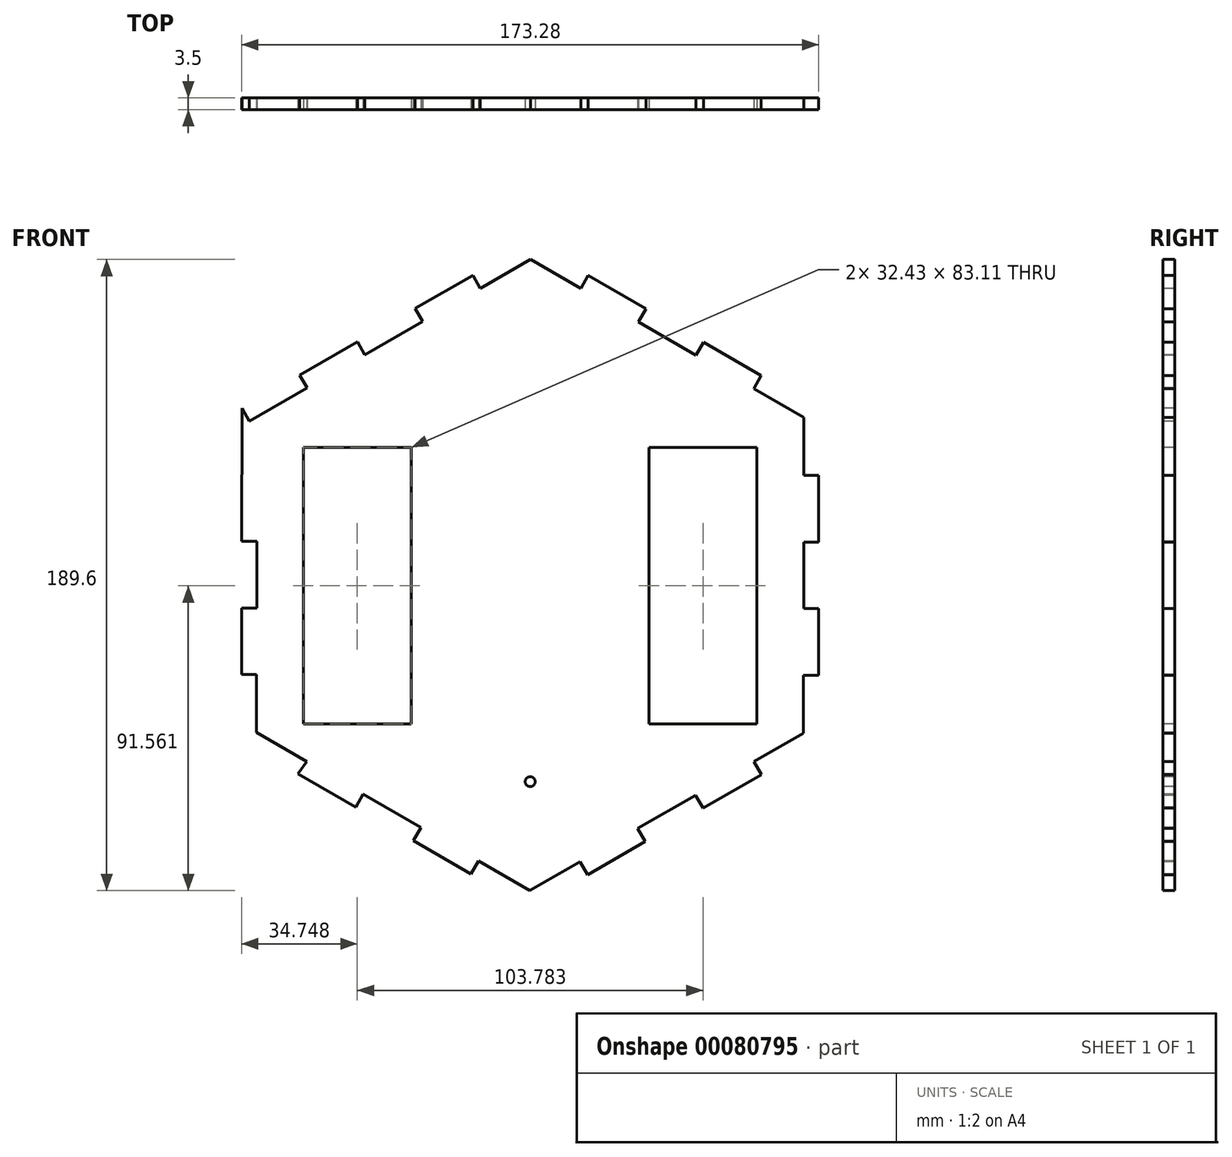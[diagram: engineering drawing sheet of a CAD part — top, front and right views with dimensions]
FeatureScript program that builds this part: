
annotation { "Feature Type Name" : "Feature", "Feature Type Description" : "" }
export const myFeature = defineFeature(function(context is Context, id is Id, definition is map)
    precondition{}
    {
        {
            var Q0;
            Q0=qCreatedBy(makeId("Front.planeOp"),FACE);
            var sketch = newSketch(context, id + "F0", { "sketchPlane" : qUnion([Q0])});
            skCircle(sketch, "E0.cCircle", {"center": v(0, 0) * mm, "radius": 86.6 * mm, "construction": true});
            skLineSegment(sketch, "E0.0", {"start": v(-86.54, 50.12) * mm, "end": v(0.13, 100) * mm});
            skLineSegment(sketch, "E0.1", {"start": v(0.13, 100) * mm, "end": v(86.67, 49.88) * mm});
            skLineSegment(sketch, "E0.2", {"start": v(86.67, 49.88) * mm, "end": v(86.54, -50.12) * mm});
            skLineSegment(sketch, "E0.3", {"start": v(86.54, -50.12) * mm, "end": v(-0.13, -100) * mm});
            skLineSegment(sketch, "E0.4", {"start": v(-0.13, -100) * mm, "end": v(-86.67, -49.88) * mm});
            skLineSegment(sketch, "E0.5", {"start": v(-86.67, -49.88) * mm, "end": v(-86.54, 50.12) * mm});
            skPoint(sketch, "E0.0.midPoint", {"position": v(-43.2, 75.06) * mm});
            skSolve(sketch);
        }
        {
            var Q0;
            Q0=makeQuery(id+"F0.imprint","IMPRINT",FACE,{"disambiguationData":[TD([[makeQuery(id+"F0.imprint","IMPRINT",EDGE,{"derivedFrom":sQuery(id+"F0.wireOp",EDGE,"E0.0")}),-1.0]])]});
            extrude(context, id + "F1", {"entities" : qUnion([Q0]), "depth" : 3.5 * mm});
        }
        {
            var Q0;
            Q0=makeQuery(id+"F1.opExtrude","CAP_FACE",FACE,{"disambiguationData":[OSD([sQuery(id+"F0.wireOp",EDGE,"E0.0"),sQuery(id+"F0.wireOp",EDGE,"E0.1"),sQuery(id+"F0.wireOp",EDGE,"E0.2"),sQuery(id+"F0.wireOp",EDGE,"E0.3"),sQuery(id+"F0.wireOp",EDGE,"E0.4"),sQuery(id+"F0.wireOp",EDGE,"E0.5")])],"isStart":false});
            var sketch = newSketch(context, id + "F2", { "sketchPlane" : qUnion([Q0])});
            skLineSegment(sketch, "E1", {"start": v(-86.54, 50.12) * mm, "end": v(-84.3, 46.22) * mm});
            skLineSegment(sketch, "E2", {"start": v(-84.3, 46.22) * mm, "end": v(-66.96, 56.2) * mm});
            skLineSegment(sketch, "E3", {"start": v(-66.96, 56.2) * mm, "end": v(-69.2, 60.1) * mm});
            skLineSegment(sketch, "E4", {"start": v(-69.2, 60.1) * mm, "end": v(-51.87, 70.07) * mm});
            skLineSegment(sketch, "E5", {"start": v(-51.87, 70.07) * mm, "end": v(-49.62, 66.17) * mm});
            skLineSegment(sketch, "E6", {"start": v(-49.62, 66.17) * mm, "end": v(-32.29, 76.15) * mm});
            skLineSegment(sketch, "E7", {"start": v(-32.29, 76.15) * mm, "end": v(-34.53, 80.05) * mm});
            skLineSegment(sketch, "E8", {"start": v(-34.53, 80.05) * mm, "end": v(-17.2, 90.02) * mm});
            skLineSegment(sketch, "E9", {"start": v(-17.2, 90.02) * mm, "end": v(-17.2, 90.02) * mm});
            skLineSegment(sketch, "E10", {"start": v(-17.2, 90.02) * mm, "end": v(0.13, 100) * mm});
            skLineSegment(sketch, "E11", {"start": v(0.13, 100) * mm, "end": v(2.38, 96.1) * mm});
            skLineSegment(sketch, "E12", {"start": v(-17.2, 90.02) * mm, "end": v(-14.95, 86.12) * mm});
            skLineSegment(sketch, "E13", {"start": v(-14.95, 86.12) * mm, "end": v(2.38, 96.1) * mm});
            skLineSegment(sketch, "E14", {"start": v(-86.67, -49.88) * mm, "end": v(-82.14, -49.89) * mm});
            skLineSegment(sketch, "E15", {"start": v(-82.14, -49.89) * mm, "end": v(-82.14, -29.89) * mm});
            skLineSegment(sketch, "E16", {"start": v(-82.14, -29.89) * mm, "end": v(-86.64, -29.88) * mm});
            skLineSegment(sketch, "E17", {"start": v(-86.64, -29.88) * mm, "end": v(-86.62, -9.88) * mm});
            skLineSegment(sketch, "E18", {"start": v(-86.6, 0) * mm, "end": v(-86.58, 20) * mm});
            skLineSegment(sketch, "E19", {"start": v(-81.27, 30.12) * mm, "end": v(-86.56, 30.12) * mm});
            skLineSegment(sketch, "E20", {"start": v(-86.67, -49.88) * mm, "end": v(-86.67, -49.88) * mm});
            skLineSegment(sketch, "E21", {"start": v(-86.56, 30.12) * mm, "end": v(-86.54, 50.12) * mm});
            skLineSegment(sketch, "E22", {"start": v(-86.62, -9.88) * mm, "end": v(-82.12, -9.89) * mm});
            skLineSegment(sketch, "E23", {"start": v(-82.12, -9.89) * mm, "end": v(-82.12, 10.11) * mm});
            skLineSegment(sketch, "E24", {"start": v(-82.12, 10.11) * mm, "end": v(-86.59, 10.12) * mm});
            skLineSegment(sketch, "E25", {"start": v(-86.59, 10.12) * mm, "end": v(-86.56, 30.12) * mm});
            skLineSegment(sketch, "E26", {"start": v(-86.56, 30.12) * mm, "end": v(-82.06, 30.11) * mm});
            skLineSegment(sketch, "E27", {"start": v(-82.06, 30.11) * mm, "end": v(-82.06, 50.11) * mm});
            skLineSegment(sketch, "E28", {"start": v(-82.06, 50.11) * mm, "end": v(-86.54, 50.11) * mm});
            skLineSegment(sketch, "E29", {"start": v(-86.54, 50.11) * mm, "end": v(-86.54, 50.12) * mm});
            skLineSegment(sketch, "E30", {"start": v(86.54, -50.12) * mm, "end": v(82.06, -50.11) * mm});
            skLineSegment(sketch, "E31", {"start": v(82.06, -50.11) * mm, "end": v(82.06, -30.11) * mm});
            skLineSegment(sketch, "E32", {"start": v(82.06, -30.11) * mm, "end": v(86.56, -30.11) * mm});
            skLineSegment(sketch, "E33", {"start": v(86.56, -30.11) * mm, "end": v(86.59, -10.11) * mm});
            skLineSegment(sketch, "E34", {"start": v(86.59, -10.11) * mm, "end": v(82.09, -10.1) * mm});
            skLineSegment(sketch, "E35", {"start": v(82.09, -10.1) * mm, "end": v(82.09, 9.9) * mm});
            skLineSegment(sketch, "E36", {"start": v(82.09, 9.9) * mm, "end": v(86.62, 9.89) * mm});
            skLineSegment(sketch, "E37", {"start": v(86.62, 9.89) * mm, "end": v(86.64, 29.89) * mm});
            skLineSegment(sketch, "E38", {"start": v(86.64, 29.89) * mm, "end": v(82.14, 29.9) * mm});
            skLineSegment(sketch, "E39", {"start": v(82.14, 29.9) * mm, "end": v(82.14, 49.9) * mm});
            skLineSegment(sketch, "E40", {"start": v(82.14, 49.9) * mm, "end": v(86.67, 49.89) * mm});
            skLineSegment(sketch, "E41", {"start": v(86.67, 49.88) * mm, "end": v(86.67, 49.89) * mm});
            skLineSegment(sketch, "E42", {"start": v(86.54, -50.12) * mm, "end": v(86.54, -50.12) * mm});
            skLineSegment(sketch, "E43", {"start": v(43.43, 74.93) * mm, "end": v(0.13, 100) * mm});
            skLineSegment(sketch, "E44", {"start": v(86.67, 49.89) * mm, "end": v(84.41, 46) * mm});
            skLineSegment(sketch, "E45", {"start": v(84.41, 46) * mm, "end": v(67.1, 56.01) * mm});
            skLineSegment(sketch, "E46", {"start": v(67.1, 56.01) * mm, "end": v(69.36, 59.9) * mm});
            skLineSegment(sketch, "E47", {"start": v(69.36, 59.9) * mm, "end": v(52.05, 69.93) * mm});
            skLineSegment(sketch, "E48", {"start": v(52.05, 69.93) * mm, "end": v(49.8, 66.04) * mm});
            skLineSegment(sketch, "E49", {"start": v(49.8, 66.04) * mm, "end": v(32.5, 76.06) * mm});
            skLineSegment(sketch, "E50", {"start": v(32.5, 76.06) * mm, "end": v(34.75, 79.95) * mm});
            skLineSegment(sketch, "E51", {"start": v(34.75, 79.95) * mm, "end": v(17.44, 89.98) * mm});
            skLineSegment(sketch, "E52", {"start": v(17.44, 89.98) * mm, "end": v(15.18, 86.08) * mm});
            skLineSegment(sketch, "E53", {"start": v(15.18, 86.08) * mm, "end": v(-2.12, 96.1) * mm});
            skLineSegment(sketch, "E54", {"start": v(-2.12, 96.1) * mm, "end": v(0.13, 100) * mm});
            skLineSegment(sketch, "E55", {"start": v(-86.67, -49.88) * mm, "end": v(-84.41, -45.99) * mm});
            skLineSegment(sketch, "E56", {"start": v(-84.41, -45.99) * mm, "end": v(-67.1, -56.01) * mm});
            skLineSegment(sketch, "E57", {"start": v(-67.1, -56.01) * mm, "end": v(-69.7, -59.7) * mm});
            skLineSegment(sketch, "E58", {"start": v(-69.7, -59.7) * mm, "end": v(-52.4, -69.73) * mm});
            skLineSegment(sketch, "E59", {"start": v(-52.4, -69.73) * mm, "end": v(-50.13, -65.83) * mm});
            skLineSegment(sketch, "E60", {"start": v(-50.13, -65.83) * mm, "end": v(-32.83, -75.86) * mm});
            skLineSegment(sketch, "E61", {"start": v(-32.83, -75.86) * mm, "end": v(-35.09, -79.76) * mm});
            skLineSegment(sketch, "E62", {"start": v(-35.09, -79.76) * mm, "end": v(-17.78, -89.78) * mm});
            skLineSegment(sketch, "E63", {"start": v(-17.78, -89.78) * mm, "end": v(-15.52, -85.89) * mm});
            skLineSegment(sketch, "E64", {"start": v(-15.52, -85.89) * mm, "end": v(1.78, -95.91) * mm});
            skLineSegment(sketch, "E65", {"start": v(1.78, -95.91) * mm, "end": v(-0.47, -99.8) * mm});
            skLineSegment(sketch, "E66", {"start": v(-0.47, -99.8) * mm, "end": v(-0.13, -100) * mm});
            skLineSegment(sketch, "E67", {"start": v(-0.13, -100) * mm, "end": v(-2.38, -96.1) * mm});
            skLineSegment(sketch, "E68", {"start": v(-2.38, -96.1) * mm, "end": v(14.95, -86.12) * mm});
            skLineSegment(sketch, "E69", {"start": v(14.95, -86.12) * mm, "end": v(17.2, -90.02) * mm});
            skLineSegment(sketch, "E70", {"start": v(17.2, -90.02) * mm, "end": v(34.53, -80.05) * mm});
            skLineSegment(sketch, "E71", {"start": v(34.53, -80.05) * mm, "end": v(32.29, -76.15) * mm});
            skLineSegment(sketch, "E72", {"start": v(32.29, -76.15) * mm, "end": v(49.62, -66.17) * mm});
            skLineSegment(sketch, "E73", {"start": v(49.62, -66.17) * mm, "end": v(51.87, -70.07) * mm});
            skLineSegment(sketch, "E74", {"start": v(52.12, -69.93) * mm, "end": v(69.45, -59.95) * mm});
            skLineSegment(sketch, "E75", {"start": v(69.45, -59.95) * mm, "end": v(67.2, -56.05) * mm});
            skLineSegment(sketch, "E76", {"start": v(67.2, -56.05) * mm, "end": v(84.54, -46.07) * mm});
            skLineSegment(sketch, "E77", {"start": v(84.54, -46.07) * mm, "end": v(86.78, -49.97) * mm});
            skPoint(sketch, "E78.firstSnap0", {"position": v(-75.62, 51.2) * mm});
            skLineSegment(sketch, "E79.bottom", {"start": v(-68.1, 38.31) * mm, "end": v(-35.68, 38.31) * mm});
            skLineSegment(sketch, "E79.top", {"start": v(-68.1, -44.8) * mm, "end": v(-35.68, -44.8) * mm});
            skLineSegment(sketch, "E79.left", {"start": v(-68.1, 38.31) * mm, "end": v(-68.1, -44.8) * mm});
            skLineSegment(sketch, "E79.right", {"start": v(-35.68, 38.31) * mm, "end": v(-35.68, -44.8) * mm});
            skLineSegment(sketch, "E80.MirrorCS", {"start": v(35.68, 38.31) * mm, "end": v(35.68, -44.8) * mm});
            skLineSegment(sketch, "E81.MirrorCS", {"start": v(68.1, 38.31) * mm, "end": v(35.68, 38.31) * mm});
            skLineSegment(sketch, "E82.MirrorCS", {"start": v(68.1, 38.31) * mm, "end": v(68.1, -44.8) * mm});
            skLineSegment(sketch, "E83.MirrorCS", {"start": v(68.1, -44.8) * mm, "end": v(35.68, -44.8) * mm});
            skCircle(sketch, "E84", {"center": v(0, -62.08) * mm, "radius": 1.5 * mm});
            skSolve(sketch);
        }
        {
            var Q0;
            Q0=makeQuery(id+"F2.imprint","IMPRINT",FACE,{"disambiguationData":[TD([[makeQuery(id+"F2.imprint","IMPRINT",EDGE,{"derivedFrom":sQuery(id+"F2.wireOp",EDGE,"E79.bottom")}),-1.0]])]});
            var Q1;
            Q1=makeQuery(id+"F2.imprint","IMPRINT",FACE,{"disambiguationData":[TD([[makeQuery(id+"F2.imprint","IMPRINT",EDGE,{"derivedFrom":sQuery(id+"F2.wireOp",EDGE,"E80.MirrorCS")}),1.0]])]});
            var Q2;
            {var subQ0=sQuery(id+"F2.wireOp",EDGE,"E46");Q2=makeQuery(id+"F2.imprint","IMPRINT",FACE,{"disambiguationData":[TD([[makeQuery(id+"F2.imprint","IMPRINT",EDGE,{"derivedFrom":subQ0}),-1.0]])]});}
            var Q3;
            {var subQ7=sQuery(id+"F2.wireOp",EDGE,"E38");Q3=makeQuery(id+"F2.imprint","IMPRINT",FACE,{"disambiguationData":[TD([[makeQuery(id+"F2.imprint","IMPRINT",EDGE,{"derivedFrom":subQ7}),-1.0]])]});}
            var Q4;
            {var subQ0=sQuery(id+"F2.wireOp",EDGE,"E34");Q4=makeQuery(id+"F2.imprint","IMPRINT",FACE,{"disambiguationData":[TD([[makeQuery(id+"F2.imprint","IMPRINT",EDGE,{"derivedFrom":subQ0}),-1.0]])]});}
            var Q5;
            {var subQ4=sQuery(id+"F2.wireOp",EDGE,"E30");Q5=makeQuery(id+"F2.imprint","IMPRINT",FACE,{"disambiguationData":[TD([[makeQuery(id+"F2.imprint","IMPRINT",EDGE,{"derivedFrom":subQ4}),1.0]])]});}
            var Q6;
            {var subQ7=sQuery(id+"F2.wireOp",EDGE,"E32");Q6=makeQuery(id+"F2.imprint","IMPRINT",FACE,{"disambiguationData":[TD([[makeQuery(id+"F2.imprint","IMPRINT",EDGE,{"derivedFrom":subQ7}),-1.0]])]});}
            var Q7;
            {var subQ0=sQuery(id+"F2.wireOp",EDGE,"E71");Q7=makeQuery(id+"F2.imprint","IMPRINT",FACE,{"disambiguationData":[TD([[makeQuery(id+"F2.imprint","IMPRINT",EDGE,{"derivedFrom":subQ0}),-1.0]])]});}
            var Q8;
            {var subQ8=sQuery(id+"F2.wireOp",EDGE,"E63");Q8=makeQuery(id+"F2.imprint","IMPRINT",FACE,{"disambiguationData":[TD([[makeQuery(id+"F2.imprint","IMPRINT",EDGE,{"derivedFrom":subQ8}),-1.0]])]});}
            var Q9;
            {var subQ2=sQuery(id+"F2.wireOp",EDGE,"E14");Q9=makeQuery(id+"F2.imprint","IMPRINT",FACE,{"disambiguationData":[TD([[makeQuery(id+"F2.imprint","IMPRINT",EDGE,{"derivedFrom":subQ2}),-1.0]])]});}
            var Q10;
            {var subQ4=sQuery(id+"F2.wireOp",EDGE,"E16");Q10=makeQuery(id+"F2.imprint","IMPRINT",FACE,{"disambiguationData":[TD([[makeQuery(id+"F2.imprint","IMPRINT",EDGE,{"derivedFrom":subQ4}),1.0]])]});}
            var Q11;
            {var subQ1=sQuery(id+"F2.wireOp",EDGE,"E18");Q11=makeQuery(id+"F2.imprint","IMPRINT",FACE,{"disambiguationData":[TD([[makeQuery(id+"F2.imprint","IMPRINT",EDGE,{"derivedFrom":subQ1}),-1.0]])]});}
            var Q12;
            {var subQ0=sQuery(id+"F2.wireOp",EDGE,"E21");Q12=makeQuery(id+"F2.imprint","IMPRINT",FACE,{"disambiguationData":[TD([[makeQuery(id+"F2.imprint","IMPRINT",EDGE,{"derivedFrom":subQ0}),-1.0]])]});}
            var Q13;
            {var subQ5=sQuery(id+"F2.wireOp",EDGE,"E3");Q13=makeQuery(id+"F2.imprint","IMPRINT",FACE,{"disambiguationData":[TD([[makeQuery(id+"F2.imprint","IMPRINT",EDGE,{"derivedFrom":subQ5}),1.0]])]});}
            var Q14;
            {var subQ0=sQuery(id+"F2.wireOp",EDGE,"E5");Q14=makeQuery(id+"F2.imprint","IMPRINT",FACE,{"disambiguationData":[TD([[makeQuery(id+"F2.imprint","IMPRINT",EDGE,{"derivedFrom":subQ0}),1.0]])]});}
            var Q15;
            Q15=makeQuery(id+"F2.imprint","IMPRINT",FACE,{"disambiguationData":[TD([[makeQuery(id+"F2.imprint","IMPRINT",EDGE,{"derivedFrom":sQuery(id+"F2.wireOp",EDGE,"E10")}),-1.0]])]});
            var Q16;
            {var subQ2=sQuery(id+"F2.wireOp",EDGE,"E11");Q16=makeQuery(id+"F2.imprint","IMPRINT",FACE,{"disambiguationData":[TD([[makeQuery(id+"F2.imprint","IMPRINT",EDGE,{"derivedFrom":subQ2}),1.0]])]});}
            var Q17;
            {var subQ1=sQuery(id+"F2.wireOp",EDGE,"E48");Q17=makeQuery(id+"F2.imprint","IMPRINT",FACE,{"disambiguationData":[TD([[makeQuery(id+"F2.imprint","IMPRINT",EDGE,{"derivedFrom":subQ1}),-1.0]])]});}
            var Q18;
            {var subQ0=sQuery(id+"F2.wireOp",EDGE,"E59");Q18=makeQuery(id+"F2.imprint","IMPRINT",FACE,{"disambiguationData":[TD([[makeQuery(id+"F2.imprint","IMPRINT",EDGE,{"derivedFrom":subQ0}),-1.0]])]});}
            var Q19;
            {var subQ0=sQuery(id+"F2.wireOp",EDGE,"E14");Q19=makeQuery(id+"F2.imprint","IMPRINT",FACE,{"disambiguationData":[TD([[makeQuery(id+"F2.imprint","IMPRINT",EDGE,{"derivedFrom":subQ0}),1.0]])]});}
            var Q20;
            {var subQ0=sQuery(id+"F2.wireOp",EDGE,"E2");var subQ1=sQuery(id+"F2.wireOp",EDGE,"E1");var subQ2=makeQuery(id+"F2.imprint","INTERSECT",VERTEX,{"derivedFrom":[subQ1,subQ0]});Q20=makeQuery(id+"F2.imprint","IMPRINT",FACE,{"disambiguationData":[TD([[makeQuery(id+"F2.imprint","IMPRINT",EDGE,{"disambiguationData":[TD([[subQ2,1.0]])],"derivedFrom":subQ1}),1.0]])]});}
            var Q21;
            {var subQ0=sQuery(id+"F2.wireOp",EDGE,"E11");Q21=makeQuery(id+"F2.imprint","IMPRINT",FACE,{"disambiguationData":[TD([[makeQuery(id+"F2.imprint","IMPRINT",EDGE,{"derivedFrom":subQ0}),-1.0]])]});}
            var Q22;
            {var subQ3=sQuery(id+"F2.wireOp",EDGE,"E39");var subQ5=sQuery(id+"F2.wireOp",EDGE,"E40");var subQ9=makeQuery(id+"F2.imprint","INTERSECT",VERTEX,{"derivedFrom":[subQ3,subQ5]});Q22=makeQuery(id+"F2.imprint","IMPRINT",FACE,{"disambiguationData":[TD([[makeQuery(id+"F2.imprint","IMPRINT",EDGE,{"disambiguationData":[TD([[subQ9,1.0]])],"derivedFrom":subQ3}),-1.0]])]});}
            var Q23;
            {var subQ7=sQuery(id+"F2.wireOp",EDGE,"E30");Q23=makeQuery(id+"F2.imprint","IMPRINT",FACE,{"disambiguationData":[TD([[makeQuery(id+"F2.imprint","IMPRINT",EDGE,{"derivedFrom":subQ7}),-1.0]])]});}
            var Q24;
            {var subQ0=sQuery(id+"F2.wireOp",EDGE,"E65");var subQ1=sQuery(id+"F2.wireOp",EDGE,"E64");var subQ2=makeQuery(id+"F2.imprint","INTERSECT",VERTEX,{"derivedFrom":[subQ1,subQ0]});Q24=makeQuery(id+"F2.imprint","IMPRINT",FACE,{"disambiguationData":[TD([[makeQuery(id+"F2.imprint","IMPRINT",EDGE,{"disambiguationData":[TD([[subQ2,1.0]])],"derivedFrom":subQ1}),-1.0]])]});}
            var Q25;
            {var subQ0=sQuery(id+"F2.wireOp",EDGE,"E69");Q25=makeQuery(id+"F2.imprint","IMPRINT",FACE,{"disambiguationData":[TD([[makeQuery(id+"F2.imprint","IMPRINT",EDGE,{"derivedFrom":subQ0}),-1.0]])]});}
            var Q26;
            {var subQ0=sQuery(id+"F2.wireOp",EDGE,"E66");Q26=makeQuery(id+"F2.imprint","IMPRINT",FACE,{"disambiguationData":[TD([[makeQuery(id+"F2.imprint","IMPRINT",EDGE,{"derivedFrom":subQ0}),-1.0]])]});}
            var Q27;
            Q27=makeQuery(id+"F2.imprint","IMPRINT",FACE,{"disambiguationData":[TD([[makeQuery(id+"F2.imprint","IMPRINT",EDGE,{"derivedFrom":sQuery(id+"F2.wireOp",EDGE,"E84")}),1.0]])]});
            extrude(context, id + "F3", {"entities" : qUnion([Q0, Q1, Q2, Q3, Q4, Q5, Q6, Q7, Q8, Q9, Q10, Q11, Q12, Q13, Q14, Q15, Q16, Q17, Q18, Q19, Q20, Q21, Q22, Q23, Q24, Q25, Q26, Q27]), "operationType" : NewBodyOperationType.REMOVE, "oppositeDirection" : true, "depth" : 25 * mm});
        }
    });
